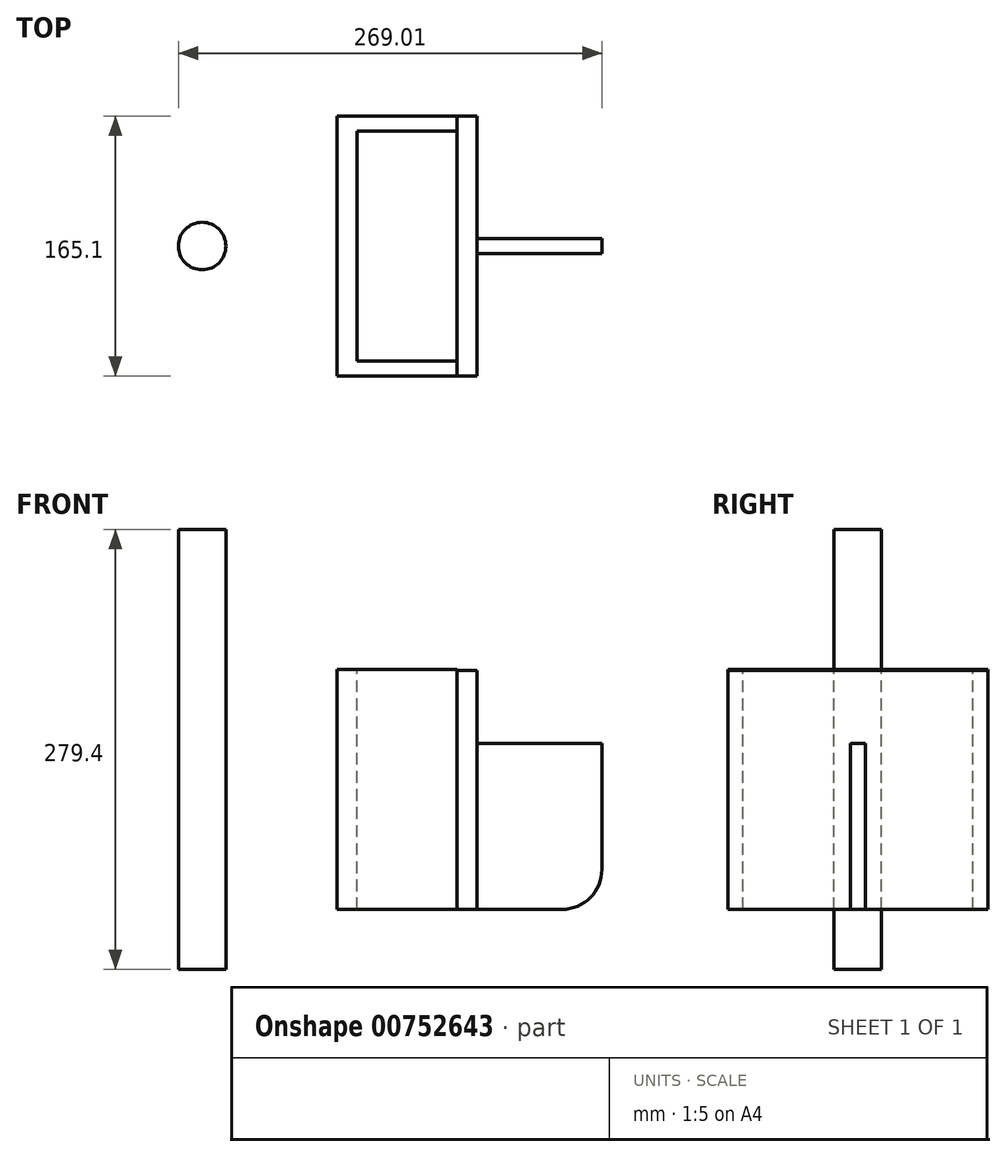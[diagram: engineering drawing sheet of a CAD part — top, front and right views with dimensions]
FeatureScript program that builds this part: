
annotation { "Feature Type Name" : "Feature", "Feature Type Description" : "" }
export const myFeature = defineFeature(function(context is Context, id is Id, definition is map)
    precondition{}
    {
        {
            var Q0;
            Q0=qCreatedBy(makeId("Right.planeOp"),FACE);
            cPlane(context, id + "F0", {"entities" : qUnion([Q0]), "cplaneType" : CPlaneType.OFFSET, "offset" : 254 * mm, "width" : 152.4 * mm, "height" : 152.4 * mm});
        }
        {
            var Q0;
            Q0=qCreatedBy(id+"F0.planeOp",FACE);
            var sketch = newSketch(context, id + "F1", { "sketchPlane" : qUnion([Q0])});
            skLineSegment(sketch, "E0.bottom", {"start": v(-82.55, 76.2) * mm, "end": v(82.55, 76.2) * mm});
            skLineSegment(sketch, "E0.top", {"start": v(-82.55, -76.2) * mm, "end": v(82.55, -76.2) * mm});
            skLineSegment(sketch, "E0.left", {"start": v(-82.55, 76.2) * mm, "end": v(-82.55, -76.2) * mm});
            skLineSegment(sketch, "E0.right", {"start": v(82.55, 76.2) * mm, "end": v(82.55, -76.2) * mm});
            skSolve(sketch);
        }
        {
            var Q0;
            Q0 = qSketchRegion(id + "F1", true);
            extrude(context, id + "F2", {"entities" : qUnion([Q0]), "oppositeDirection" : true, "depth" : 12.7 * mm, "offsetDistance" : 25.4 * mm, "hasSecondDirection" : true, "secondDirectionOppositeDirection" : false, "secondDirectionDepth" : 63.5 * mm});
        }
        {
            var Q0;
            Q0=makeQuery(id+"F2.opExtrude","SWEPT_FACE",FACE,{"disambiguationData":[OSD([sQuery(id+"F1.wireOp",EDGE,"E0.bottom")])]});
            var sketch = newSketch(context, id + "F3", { "sketchPlane" : qUnion([Q0])});
            skCircle(sketch, "E1", {"center": v(155.58, 0) * mm, "radius": 15.08 * mm});
            skSolve(sketch);
        }
        {
            var Q0;
            Q0 = qSketchRegion(id + "F3", true);
            extrude(context, id + "F4", {"entities" : qUnion([Q0]), "oppositeDirection" : true, "depth" : 190.5 * mm, "offsetDistance" : 25.4 * mm, "hasSecondDirection" : true, "secondDirectionOppositeDirection" : false, "secondDirectionDepth" : 88.9 * mm});
        }
        {
            var Q0;
            Q0=makeQuery(id+"F2.opExtrude","SWEPT_FACE",FACE,{"disambiguationData":[OSD([sQuery(id+"F1.wireOp",EDGE,"E0.bottom")])]});
            var sketch = newSketch(context, id + "F5", { "sketchPlane" : qUnion([Q0])});
            skLineSegment(sketch, "E2.bottom", {"start": v(317.5, -73.03) * mm, "end": v(254, -73.03) * mm});
            skLineSegment(sketch, "E2.top", {"start": v(317.5, 73.03) * mm, "end": v(254, 73.02) * mm});
            skLineSegment(sketch, "E2.left", {"start": v(317.5, -73.03) * mm, "end": v(317.5, 73.03) * mm});
            skLineSegment(sketch, "E2.right", {"start": v(254, -73.03) * mm, "end": v(254, 73.03) * mm});
            skSolve(sketch);
        }
        {
            var Q0;
            Q0 = qSketchRegion(id + "F5", true);
            extrude(context, id + "F6", {"entities" : qUnion([Q0]), "operationType" : NewBodyOperationType.REMOVE, "endBound" : BoundingType.THROUGH_ALL, "oppositeDirection" : true, "depth" : 25.4 * mm, "offsetDistance" : 25.4 * mm});
        }
        {
            var Q0;
            {var subQ0=sQuery(id+"F1.wireOp",EDGE,"E0.bottom");var subQ1=sQuery(id+"F1.wireOp",EDGE,"E0.top");var subQ2=sQuery(id+"F1.wireOp",EDGE,"E0.left");Q0=makeQuery(id+"F6.boolean.opBoolean","SPLIT",FACE,{"disambiguationData":[TD([makeQuery(id+"F2.opExtrude","SWEPT_FACE",FACE,{"disambiguationData":[OSD([subQ2])]})])],"derivedFrom":makeQuery(id+"F2.opExtrude","CAP_FACE",FACE,{"disambiguationData":[OSD([subQ0,subQ1,subQ2,sQuery(id+"F1.wireOp",EDGE,"E0.right")])],"isStart":true})});}
            var sketch = newSketch(context, id + "F7", { "sketchPlane" : qUnion([Q0])});
            skLineSegment(sketch, "E3.bottom", {"start": v(-82.55, -76.2) * mm, "end": v(82.55, -76.2) * mm});
            skLineSegment(sketch, "E3.top", {"start": v(-82.55, 75.72) * mm, "end": v(82.55, 75.72) * mm});
            skLineSegment(sketch, "E3.left", {"start": v(-82.55, -76.2) * mm, "end": v(-82.55, 75.72) * mm});
            skLineSegment(sketch, "E3.right", {"start": v(82.55, -76.2) * mm, "end": v(82.55, 75.72) * mm});
            skSolve(sketch);
        }
        {
            var Q0;
            Q0 = qSketchRegion(id + "F7", true);
            extrude(context, id + "F8", {"entities" : qUnion([Q0]), "depth" : 12.7 * mm, "offsetDistance" : 25.4 * mm});
        }
        {
            var Q0;
            Q0=qCreatedBy(makeId("Front.planeOp"),FACE);
            var sketch = newSketch(context, id + "F9", { "sketchPlane" : qUnion([Q0])});
            skLineSegment(sketch, "E4.bottom", {"start": v(330.2, -76.2) * mm, "end": v(384.1, -76.2) * mm});
            skLineSegment(sketch, "E4.top", {"start": v(330.2, 29.4) * mm, "end": v(409.5, 29.4) * mm});
            skLineSegment(sketch, "E4.left", {"start": v(330.2, -76.2) * mm, "end": v(330.2, 29.4) * mm});
            skLineSegment(sketch, "E4.right", {"start": v(409.5, -50.8) * mm, "end": v(409.5, 29.4) * mm});
            skPoint(sketch, "E5.visualSharp", {"position": v(409.5, -76.2) * mm});
            skArc(sketch, "E5.filletArc", {"start": v(384.1, -76.2) * mm, "mid": v(402.06, -68.76) * mm, "end": v(409.5, -50.8) * mm});
            skSolve(sketch);
        }
        {
            var Q0;
            Q0 = qSketchRegion(id + "F9", true);
            extrude(context, id + "F10", {"entities" : qUnion([Q0]), "depth" : 4.76 * mm, "offsetDistance" : 25.4 * mm, "hasSecondDirection" : true, "secondDirectionOppositeDirection" : true, "secondDirectionDepth" : 4.76 * mm});
        }
    });
